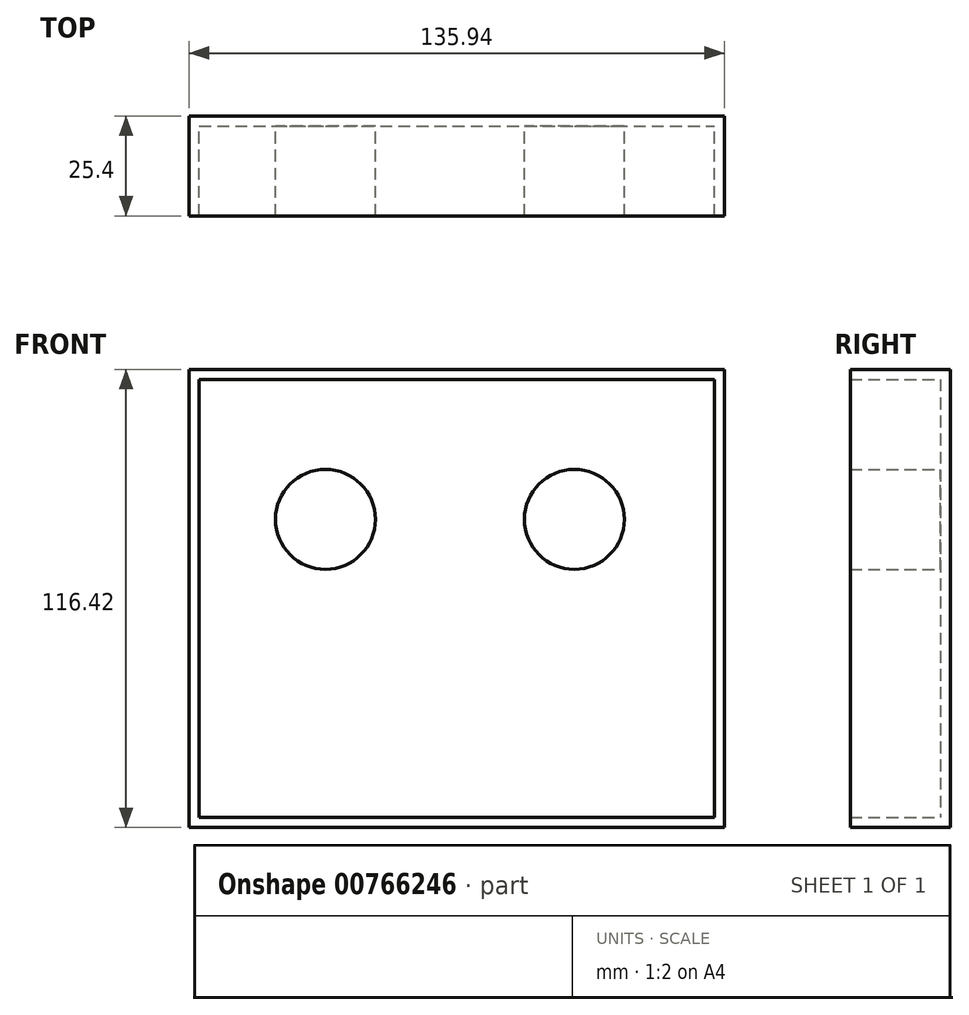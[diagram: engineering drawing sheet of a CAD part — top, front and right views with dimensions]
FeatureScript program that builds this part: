
annotation { "Feature Type Name" : "Feature", "Feature Type Description" : "" }
export const myFeature = defineFeature(function(context is Context, id is Id, definition is map)
    precondition{}
    {
        {
            var Q0;
            Q0=qCreatedBy(makeId("Front.planeOp"),FACE);
            var sketch = newSketch(context, id + "F0", { "sketchPlane" : qUnion([Q0])});
            skLineSegment(sketch, "E0.bottom", {"start": v(-72.71, 61.15) * mm, "end": v(63.23, 61.15) * mm});
            skLineSegment(sketch, "E0.top", {"start": v(-72.71, -55.27) * mm, "end": v(63.23, -55.27) * mm});
            skLineSegment(sketch, "E0.left", {"start": v(-72.71, 61.15) * mm, "end": v(-72.71, -55.27) * mm});
            skLineSegment(sketch, "E0.right", {"start": v(63.23, 61.15) * mm, "end": v(63.23, -55.27) * mm});
            skSolve(sketch);
        }
        {
            var Q0;
            Q0=makeQuery(id+"F0.imprint","IMPRINT",FACE,{"disambiguationData":[TD([[makeQuery(id+"F0.imprint","IMPRINT",EDGE,{"derivedFrom":sQuery(id+"F0.wireOp",EDGE,"E0.bottom")}),-1.0]])]});
            extrude(context, id + "F1", {"entities" : qUnion([Q0]), "depth" : 25.4 * mm, "offsetDistance" : 25.4 * mm});
        }
        {
            var Q0;
            Q0=makeQuery(id+"F1.opExtrude","CAP_FACE",FACE,{"disambiguationData":[OSD([sQuery(id+"F0.wireOp",EDGE,"E0.bottom"),sQuery(id+"F0.wireOp",EDGE,"E0.top"),sQuery(id+"F0.wireOp",EDGE,"E0.left"),sQuery(id+"F0.wireOp",EDGE,"E0.right")])],"isStart":false});
            shell(context, id + "F2", {"entities" : qUnion([Q0]), "thickness" : 2.54 * mm});
        }
        {
            var Q0;
            Q0=qCreatedBy(makeId("Front.planeOp"),FACE);
            var sketch = newSketch(context, id + "F3", { "sketchPlane" : qUnion([Q0])});
            skCircle(sketch, "E1", {"center": v(-38.1, 23.05) * mm, "radius": 12.7 * mm});
            skSolve(sketch);
        }
        {
            var Q0;
            Q0 = qSketchRegion(id + "F3", true);
            extrude(context, id + "F4", {"entities" : qUnion([Q0]), "operationType" : NewBodyOperationType.ADD, "depth" : 25.4 * mm, "offsetDistance" : 25.4 * mm});
        }
        {
            var Q0;
            Q0=qCreatedBy(makeId("Front.planeOp"),FACE);
            var sketch = newSketch(context, id + "F5", { "sketchPlane" : qUnion([Q0])});
            skCircle(sketch, "E2", {"center": v(25.13, 23.05) * mm, "radius": 12.7 * mm});
            skSolve(sketch);
        }
        {
            var Q0;
            Q0 = qSketchRegion(id + "F5", true);
            extrude(context, id + "F6", {"entities" : qUnion([Q0]), "operationType" : NewBodyOperationType.ADD, "depth" : 25.4 * mm, "offsetDistance" : 25.4 * mm});
        }
    });
